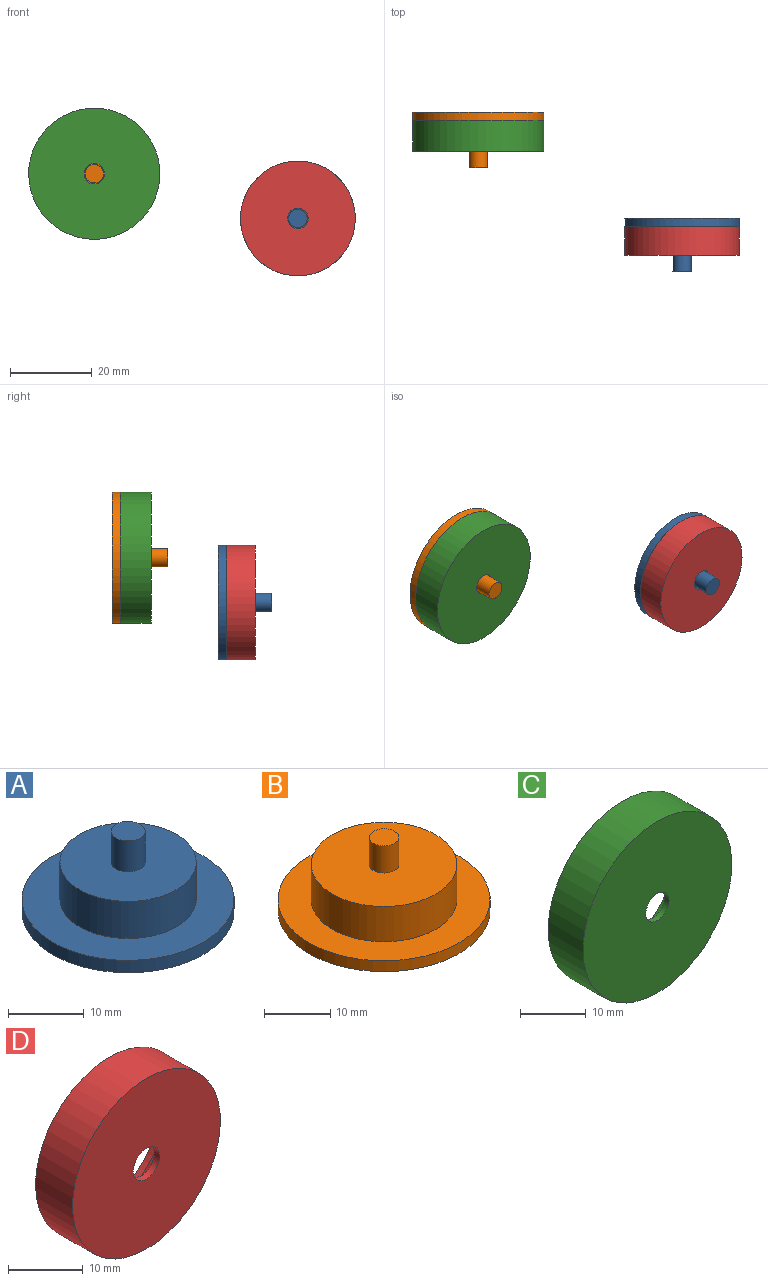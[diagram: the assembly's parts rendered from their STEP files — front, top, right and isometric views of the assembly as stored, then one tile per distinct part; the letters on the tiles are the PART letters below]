
ASSEMBLY  parts=4 mates=2
PART A: 7 faces, bbox 28x28x13 mm
  f0: cylinder r=9mm len=18mm, axis (0,0,-1), area 339.3mm2, adj f1,f5
  f1: plane 18x18mm, normal (0,0,1), area 238.6mm2, adj f0,f2
  f2: cylinder r=2.25mm len=5mm, axis (0,0,-1), area 70.7mm2, adj f1,f3
  f3: plane 4.5x4.5mm, normal (0,0,1), area 15.9mm2, adj f2
  f4: cylinder r=14mm len=28mm, axis (0,0,-1), area 175.9mm2, adj f5,f6
  f5: plane 28x28mm, normal (0,0,1), area 361.3mm2, adj f0,f4
  f6: plane 28x28mm, normal (0,0,-1), area 615.8mm2, adj f4
PART B: 7 faces, bbox 32x32x13.5 mm
  f0: cylinder r=11mm len=22mm, axis (0,0,-1), area 449.2mm2, adj f1,f5
  f1: plane 22x22mm, normal (0,0,1), area 364.2mm2, adj f0,f2
  f2: cylinder r=2.25mm len=5mm, axis (0,0,-1), area 70.7mm2, adj f1,f3
  f3: plane 4.5x4.5mm, normal (0,0,1), area 15.9mm2, adj f2
  f4: cylinder r=16mm len=32mm, axis (0,0,-1), area 201.1mm2, adj f5,f6
  f5: plane 32x32mm, normal (0,0,1), area 424.1mm2, adj f0,f4
  f6: plane 32x32mm, normal (0,0,-1), area 804.2mm2, adj f4
PART C: 8 faces, bbox 32x7.5x32 mm
  f0: plane 32x32mm, normal (0,-1,0), area 784.6mm2, adj f1,f7
  f1: cylinder r=16mm len=32mm, axis (0,1,0), area 754mm2, adj f0,f2
  f2: plane 32x32mm, normal (0,1,0), area 424.1mm2, adj f1,f3
  f3: cylinder r=11mm len=22mm, axis (0,1,0), area 69.1mm2, adj f2,f4
  f4: plane 28x28mm, normal (0,-1,0), area 235.6mm2, adj f3,f5
  f5: cylinder r=14mm len=28mm, axis (0,1,0), area 483.8mm2, adj f4,f6
  f6: plane 28x28mm, normal (0,1,0), area 596.1mm2, adj f5,f7
  f7: cylinder r=2.5mm len=5mm, axis (0,1,0), area 15.7mm2, adj f0,f6
PART D: 107 faces, bbox 28x7x28 mm
  f0: plane 24x23.98mm, normal (0,-1,0), area 179.5mm2, adj f2,f3,f4,f5,f6,f7,f8,f9
  f1: plane 24x23.98mm, normal (0,1,0), area 414.3mm2, adj f2,f3,f4,f5,f6,f7,f8,f9
  f2: cylinder r=12mm len=5mm, axis (0,1,0), area 7.6mm2, adj f0,f1,f101,f106
  f3: cylinder r=12mm len=5mm, axis (0,1,0), area 7.6mm2, adj f0,f1,f98,f103
  f4: cylinder r=12mm len=5mm, axis (0,1,0), area 7.6mm2, adj f0,f1,f95,f100
  f5: cylinder r=12mm len=5mm, axis (0,1,0), area 7.6mm2, adj f0,f1,f92,f97
  f6: cylinder r=12mm len=5mm, axis (0,1,0), area 7.6mm2, adj f0,f1,f89,f94
  f7: cylinder r=12mm len=5mm, axis (0,1,0), area 7.6mm2, adj f0,f1,f86,f91
  f8: cylinder r=12mm len=5mm, axis (0,1,0), area 7.6mm2, adj f0,f1,f83,f88
  f9: cylinder r=12mm len=5mm, axis (0,1,0), area 7.6mm2, adj f0,f1,f80,f85
  f10: cylinder r=12mm len=5mm, axis (0,1,0), area 7.6mm2, adj f0,f1,f77,f82
  f11: cylinder r=12mm len=5mm, axis (0,1,0), area 7.6mm2, adj f0,f1,f74,f79
  f12: cylinder r=12mm len=5mm, axis (0,1,0), area 7.6mm2, adj f0,f1,f71,f76
  f13: cylinder r=12mm len=5mm, axis (0,1,0), area 7.6mm2, adj f0,f1,f68,f73
  f14: cylinder r=12mm len=5mm, axis (0,1,0), area 7.6mm2, adj f0,f1,f65,f70
  f15: cylinder r=12mm len=5mm, axis (0,1,0), area 7.6mm2, adj f0,f1,f62,f67
  f16: cylinder r=12mm len=5mm, axis (0,1,0), area 7.6mm2, adj f0,f1,f59,f64
  f17: cylinder r=12mm len=5mm, axis (0,1,0), area 7.6mm2, adj f0,f1,f56,f61
  f18: cylinder r=12mm len=5mm, axis (0,1,0), area 7.6mm2, adj f0,f1,f53,f58
  f19: cylinder r=12mm len=5mm, axis (0,1,0), area 7.6mm2, adj f0,f1,f50,f55
  f20: cylinder r=12mm len=5mm, axis (0,1,0), area 7.6mm2, adj f0,f1,f47,f52
  f21: cylinder r=12mm len=5mm, axis (0,1,0), area 7.6mm2, adj f0,f1,f44,f49
  f22: cylinder r=12mm len=5mm, axis (0,1,0), area 7.6mm2, adj f0,f1,f41,f46
  f23: cylinder r=12mm len=5mm, axis (0,1,0), area 7.6mm2, adj f0,f1,f38,f43
  f24: cylinder r=12mm len=5mm, axis (0,1,0), area 7.6mm2, adj f0,f1,f35,f40
  f25: cylinder r=12mm len=5mm, axis (0,1,0), area 7.6mm2, adj f0,f1,f32,f37
  f26: cylinder r=12mm len=5mm, axis (0,1,0), area 7.6mm2, adj f0,f1,f33,f104
  f27: plane 28x28mm, normal (0,-1,0), area 596.1mm2, adj f28,f31
  f28: cylinder r=14mm len=28mm, axis (0,1,0), area 615.8mm2, adj f27,f29
  f29: plane 28x28mm, normal (0,1,0), area 361.3mm2, adj f28,f30
  f30: cylinder r=9mm len=18mm, axis (0,1,0), area 56.5mm2, adj f0,f29
  f31: cylinder r=2.5mm len=5mm, axis (0,1,0), area 15.7mm2, adj f1,f27
  f32: plane 5x0.47mm, normal (0.98,0,0.19), area 2.4mm2, adj f0,f1,f25,f34
  f33: plane 5x0.47mm, normal (-0.98,0,-0.19), area 2.4mm2, adj f0,f1,f26,f34
  f34: plane 5x1.47mm, normal (-0.19,0,0.98), area 7.5mm2, adj f0,f1,f32,f33
  f35: plane 5x0.43mm, normal (0.9,0,0.43), area 2.4mm2, adj f0,f1,f24,f36
  f36: plane 5x1.36mm, normal (-0.43,0,0.9), area 7.5mm2, adj f0,f1,f35,f37
  f37: plane 5x0.43mm, normal (-0.9,0,-0.43), area 2.4mm2, adj f0,f1,f25,f36
  f38: plane 5x0.37mm, normal (0.77,0,0.64), area 2.4mm2, adj f0,f1,f23,f39
  f39: plane 5x1.16mm, normal (-0.64,0,0.77), area 7.5mm2, adj f0,f1,f38,f40
  f40: plane 5x0.37mm, normal (-0.77,0,-0.64), area 2.4mm2, adj f0,f1,f24,f39
  f41: plane 5x0.39mm, normal (0.59,0,0.81), area 2.4mm2, adj f0,f1,f22,f42
  f42: plane 5x1.21mm, normal (-0.81,0,0.59), area 7.5mm2, adj f0,f1,f41,f43
  f43: plane 5x0.39mm, normal (-0.59,0,-0.81), area 2.4mm2, adj f0,f1,f23,f42
  f44: plane 5x0.44mm, normal (0.37,0,0.93), area 2.4mm2, adj f0,f1,f21,f45
  f45: plane 5x1.39mm, normal (-0.93,0,0.37), area 7.5mm2, adj f0,f1,f44,f46
  f46: plane 5x0.44mm, normal (-0.37,0,-0.93), area 2.4mm2, adj f0,f1,f22,f45
  f47: plane 5x0.47mm, normal (0.13,0,0.99), area 2.4mm2, adj f0,f1,f20,f48
  f48: plane 5x1.49mm, normal (-0.99,0,0.13), area 7.5mm2, adj f0,f1,f47,f49
  f49: plane 5x0.47mm, normal (-0.13,0,-0.99), area 2.4mm2, adj f0,f1,f21,f48
  f50: plane 5x0.47mm, normal (-0.13,0,0.99), area 2.4mm2, adj f0,f1,f19,f51
  f51: plane 5x1.49mm, normal (-0.99,0,-0.13), area 7.5mm2, adj f0,f1,f50,f52
  f52: plane 5x0.47mm, normal (0.13,0,-0.99), area 2.4mm2, adj f0,f1,f20,f51
  f53: plane 5x0.44mm, normal (-0.37,0,0.93), area 2.4mm2, adj f0,f1,f18,f54
  f54: plane 5x1.39mm, normal (-0.93,0,-0.37), area 7.5mm2, adj f0,f1,f53,f55
  f55: plane 5x0.44mm, normal (0.37,0,-0.93), area 2.4mm2, adj f0,f1,f19,f54
  f56: plane 5x0.39mm, normal (-0.59,0,0.81), area 2.4mm2, adj f0,f1,f17,f57
  f57: plane 5x1.21mm, normal (-0.81,0,-0.59), area 7.5mm2, adj f0,f1,f56,f58
  f58: plane 5x0.39mm, normal (0.59,0,-0.81), area 2.4mm2, adj f0,f1,f18,f57
  f59: plane 5x0.37mm, normal (-0.77,0,0.64), area 2.4mm2, adj f0,f1,f16,f60
  f60: plane 5x1.16mm, normal (-0.64,0,-0.77), area 7.5mm2, adj f0,f1,f59,f61
  f61: plane 5x0.37mm, normal (0.77,0,-0.64), area 2.4mm2, adj f0,f1,f17,f60
  f62: plane 5x0.43mm, normal (-0.9,0,0.43), area 2.4mm2, adj f0,f1,f15,f63
  f63: plane 5x1.36mm, normal (-0.43,0,-0.9), area 7.5mm2, adj f0,f1,f62,f64
  f64: plane 5x0.43mm, normal (0.9,0,-0.43), area 2.4mm2, adj f0,f1,f16,f63
  f65: plane 5x0.47mm, normal (-0.98,0,0.19), area 2.4mm2, adj f0,f1,f14,f66
  f66: plane 5x1.47mm, normal (-0.19,0,-0.98), area 7.5mm2, adj f0,f1,f65,f67
  f67: plane 5x0.47mm, normal (0.98,0,-0.19), area 2.4mm2, adj f0,f1,f15,f66
  f68: plane 5x0.48mm, normal (-1,0,-0.06), area 2.4mm2, adj f0,f1,f13,f69
  f69: plane 5x1.5mm, normal (0.06,0,-1), area 7.5mm2, adj f0,f1,f68,f70
  f70: plane 5x0.48mm, normal (1,0,0.06), area 2.4mm2, adj f0,f1,f14,f69
  f71: plane 5x0.45mm, normal (-0.95,0,-0.31), area 2.4mm2, adj f0,f1,f12,f72
  f72: plane 5x1.43mm, normal (0.31,0,-0.95), area 7.5mm2, adj f0,f1,f71,f73
  f73: plane 5x0.45mm, normal (0.95,0,0.31), area 2.4mm2, adj f0,f1,f13,f72
  f74: plane 5x0.4mm, normal (-0.84,0,-0.54), area 2.4mm2, adj f0,f1,f11,f75
  f75: plane 5x1.27mm, normal (0.54,0,-0.84), area 7.5mm2, adj f0,f1,f74,f76
  f76: plane 5x0.4mm, normal (0.84,0,0.54), area 2.4mm2, adj f0,f1,f12,f75
  f77: plane 5x0.35mm, normal (-0.68,0,-0.73), area 2.4mm2, adj f0,f1,f10,f78
  f78: plane 5x1.09mm, normal (0.73,0,-0.68), area 7.5mm2, adj f0,f1,f77,f79
  f79: plane 5x0.35mm, normal (0.68,0,0.73), area 2.4mm2, adj f0,f1,f11,f78
  f80: plane 5x0.42mm, normal (-0.48,0,-0.88), area 2.4mm2, adj f0,f1,f9,f81
  f81: plane 5x1.31mm, normal (0.88,0,-0.48), area 7.5mm2, adj f0,f1,f80,f82
  f82: plane 5x0.42mm, normal (0.48,0,0.88), area 2.4mm2, adj f0,f1,f10,f81
  f83: plane 5x0.46mm, normal (-0.25,0,-0.97), area 2.4mm2, adj f0,f1,f8,f84
  f84: plane 5x1.45mm, normal (0.97,0,-0.25), area 7.5mm2, adj f0,f1,f83,f85
  f85: plane 5x0.46mm, normal (0.25,0,0.97), area 2.4mm2, adj f0,f1,f9,f84
  f86: plane 5x0.48mm, normal (0,0,-1), area 2.4mm2, adj f0,f1,f7,f87
  f87: plane 5x1.5mm, normal (1,0,0), area 7.5mm2, adj f0,f1,f86,f88
  f88: plane 5x0.48mm, normal (0,0,1), area 2.4mm2, adj f0,f1,f8,f87
  f89: plane 5x0.46mm, normal (0.25,0,-0.97), area 2.4mm2, adj f0,f1,f6,f90
  f90: plane 5x1.45mm, normal (0.97,0,0.25), area 7.5mm2, adj f0,f1,f89,f91
  f91: plane 5x0.46mm, normal (-0.25,0,0.97), area 2.4mm2, adj f0,f1,f7,f90
  f92: plane 5x0.42mm, normal (0.48,0,-0.88), area 2.4mm2, adj f0,f1,f5,f93
  f93: plane 5x1.31mm, normal (0.88,0,0.48), area 7.5mm2, adj f0,f1,f92,f94
  f94: plane 5x0.42mm, normal (-0.48,0,0.88), area 2.4mm2, adj f0,f1,f6,f93
  f95: plane 5x0.35mm, normal (0.68,0,-0.73), area 2.4mm2, adj f0,f1,f4,f96
  f96: plane 5x1.09mm, normal (0.73,0,0.68), area 7.5mm2, adj f0,f1,f95,f97
  f97: plane 5x0.35mm, normal (-0.68,0,0.73), area 2.4mm2, adj f0,f1,f5,f96
  f98: plane 5x0.4mm, normal (0.84,0,-0.54), area 2.4mm2, adj f0,f1,f3,f99
  f99: plane 5x1.27mm, normal (0.54,0,0.84), area 7.5mm2, adj f0,f1,f98,f100
  f100: plane 5x0.4mm, normal (-0.84,0,0.54), area 2.4mm2, adj f0,f1,f4,f99
  f101: plane 5x0.45mm, normal (0.95,0,-0.31), area 2.4mm2, adj f0,f1,f2,f102
  f102: plane 5x1.43mm, normal (0.31,0,0.95), area 7.5mm2, adj f0,f1,f101,f103
  f103: plane 5x0.45mm, normal (-0.95,0,0.31), area 2.4mm2, adj f0,f1,f3,f102
  f104: plane 5x0.48mm, normal (1,0,-0.06), area 2.4mm2, adj f0,f1,f26,f105
  f105: plane 5x1.5mm, normal (0.06,0,1), area 7.5mm2, adj f0,f1,f104,f106
  f106: plane 5x0.48mm, normal (-1,0,0.06), area 2.4mm2, adj f0,f1,f2,f105
PLACE A rot(axis=(1,0,0),90deg) t=(38.68,9,0)mm
PLACE B rot(axis=(0.58,-0.58,0.58),120deg) t=(-11,34.9,10.91)mm
PLACE C t=(-11,25.4,10.91)mm
PLACE D t=(38.68,0,0)mm
MATE fastened A.f0 <-> D.f2  axis (0,-1,0) through (38.68,1,0)mm
MATE fastened B.f0 <-> C.f1  axis (0,-1,0) through (-11,26.4,10.91)mm
